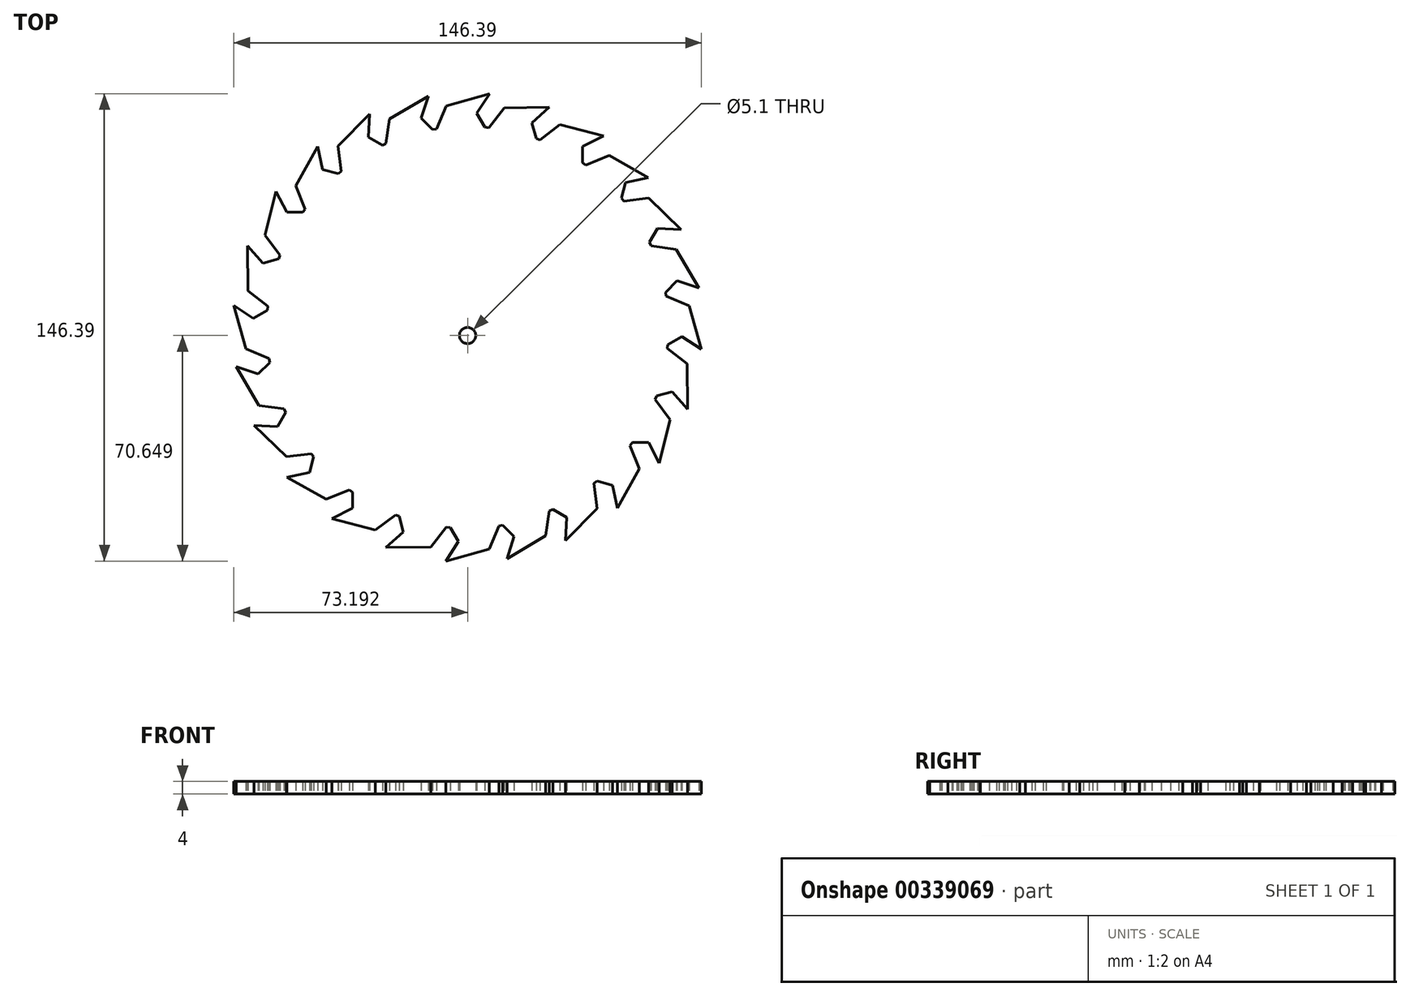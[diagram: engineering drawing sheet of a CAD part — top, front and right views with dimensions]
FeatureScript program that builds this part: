
annotation { "Feature Type Name" : "Feature", "Feature Type Description" : "" }
export const myFeature = defineFeature(function(context is Context, id is Id, definition is map)
    precondition{}
    {
        {
            var Q0;
            Q0=qCreatedBy(makeId("Top.planeOp"),FACE);
            var sketch = newSketch(context, id + "F0", { "sketchPlane" : qUnion([Q0])});
            skCircle(sketch, "E0", {"center": v(-75.15, 71.96) * mm, "radius": 61.72 * mm});
            skCircle(sketch, "E1", {"center": v(-75.15, 71.96) * mm, "radius": 2.55 * mm});
            skLineSegment(sketch, "E2", {"start": v(-121.66, 131.8) * mm, "end": v(-128.98, 118.83) * mm});
            skLineSegment(sketch, "E3", {"start": v(-128.98, 118.83) * mm, "end": v(-126.02, 111.53) * mm});
            skLineSegment(sketch, "E4", {"start": v(-126.02, 111.53) * mm, "end": v(-126.75, 110.54) * mm});
            skLineSegment(sketch, "E5", {"start": v(-126.75, 110.54) * mm, "end": v(-131.8, 110.54) * mm});
            skLineSegment(sketch, "E6", {"start": v(-131.8, 110.54) * mm, "end": v(-135.43, 117.68) * mm});
            skLineSegment(sketch, "E7.1.0", {"start": v(-134.9, 117.82) * mm, "end": v(-138.62, 103.38) * mm});
            skLineSegment(sketch, "E7.1.1", {"start": v(-138.62, 103.38) * mm, "end": v(-133.87, 97.1) * mm});
            skLineSegment(sketch, "E7.1.2", {"start": v(-134.32, 95.96) * mm, "end": v(-139.2, 94.65) * mm});
            skLineSegment(sketch, "E7.1.3", {"start": v(-133.87, 97.1) * mm, "end": v(-134.32, 95.96) * mm});
            skLineSegment(sketch, "E7.1.4", {"start": v(-139.2, 94.65) * mm, "end": v(-144.55, 100.6) * mm});
            skLineSegment(sketch, "E7.2.0", {"start": v(-144.08, 100.87) * mm, "end": v(-143.93, 85.97) * mm});
            skLineSegment(sketch, "E7.2.1", {"start": v(-143.93, 85.97) * mm, "end": v(-137.71, 81.14) * mm});
            skLineSegment(sketch, "E7.2.2", {"start": v(-137.86, 79.91) * mm, "end": v(-142.23, 77.39) * mm});
            skLineSegment(sketch, "E7.2.3", {"start": v(-137.71, 81.14) * mm, "end": v(-137.86, 79.91) * mm});
            skLineSegment(sketch, "E7.2.4", {"start": v(-142.23, 77.39) * mm, "end": v(-148.94, 81.76) * mm});
            skLineSegment(sketch, "E7.3.0", {"start": v(-148.55, 82.13) * mm, "end": v(-144.55, 67.78) * mm});
            skLineSegment(sketch, "E7.3.1", {"start": v(-144.55, 67.78) * mm, "end": v(-137.3, 64.72) * mm});
            skLineSegment(sketch, "E7.3.2", {"start": v(-137.12, 63.5) * mm, "end": v(-140.69, 59.93) * mm});
            skLineSegment(sketch, "E7.3.3", {"start": v(-137.3, 64.72) * mm, "end": v(-137.12, 63.5) * mm});
            skLineSegment(sketch, "E7.3.4", {"start": v(-140.69, 59.93) * mm, "end": v(-148.3, 62.41) * mm});
            skLineSegment(sketch, "E7.4.0", {"start": v(-148.03, 62.87) * mm, "end": v(-140.45, 50.05) * mm});
            skLineSegment(sketch, "E7.4.1", {"start": v(-140.45, 50.05) * mm, "end": v(-132.65, 48.97) * mm});
            skLineSegment(sketch, "E7.4.2", {"start": v(-132.16, 47.84) * mm, "end": v(-134.68, 43.46) * mm});
            skLineSegment(sketch, "E7.4.3", {"start": v(-132.65, 48.97) * mm, "end": v(-132.16, 47.84) * mm});
            skLineSegment(sketch, "E7.4.4", {"start": v(-134.68, 43.46) * mm, "end": v(-142.67, 43.9) * mm});
            skLineSegment(sketch, "E7.5.0", {"start": v(-142.53, 44.4) * mm, "end": v(-131.89, 33.98) * mm});
            skLineSegment(sketch, "E7.5.1", {"start": v(-131.89, 33.98) * mm, "end": v(-124.08, 34.96) * mm});
            skLineSegment(sketch, "E7.5.2", {"start": v(-123.31, 33.99) * mm, "end": v(-124.62, 29.11) * mm});
            skLineSegment(sketch, "E7.5.3", {"start": v(-124.08, 34.96) * mm, "end": v(-123.31, 33.99) * mm});
            skLineSegment(sketch, "E7.5.4", {"start": v(-124.62, 29.11) * mm, "end": v(-132.45, 27.46) * mm});
            skLineSegment(sketch, "E7.6.0", {"start": v(-132.45, 28) * mm, "end": v(-119.47, 20.67) * mm});
            skLineSegment(sketch, "E7.6.1", {"start": v(-119.47, 20.67) * mm, "end": v(-112.17, 23.64) * mm});
            skLineSegment(sketch, "E7.6.2", {"start": v(-111.18, 22.9) * mm, "end": v(-111.18, 17.86) * mm});
            skLineSegment(sketch, "E7.6.3", {"start": v(-112.17, 23.64) * mm, "end": v(-111.18, 22.9) * mm});
            skLineSegment(sketch, "E7.6.4", {"start": v(-111.18, 17.86) * mm, "end": v(-118.32, 14.23) * mm});
            skLineSegment(sketch, "E7.7.0", {"start": v(-118.45, 14.75) * mm, "end": v(-104.02, 11.04) * mm});
            skLineSegment(sketch, "E7.7.1", {"start": v(-104.02, 11.04) * mm, "end": v(-97.75, 15.79) * mm});
            skLineSegment(sketch, "E7.7.2", {"start": v(-96.6, 15.34) * mm, "end": v(-95.3, 10.46) * mm});
            skLineSegment(sketch, "E7.7.3", {"start": v(-97.75, 15.79) * mm, "end": v(-96.6, 15.34) * mm});
            skLineSegment(sketch, "E7.7.4", {"start": v(-95.3, 10.46) * mm, "end": v(-101.25, 5.11) * mm});
            skLineSegment(sketch, "E7.8.0", {"start": v(-101.51, 5.58) * mm, "end": v(-86.61, 5.73) * mm});
            skLineSegment(sketch, "E7.8.1", {"start": v(-86.61, 5.73) * mm, "end": v(-81.78, 11.94) * mm});
            skLineSegment(sketch, "E7.8.2", {"start": v(-80.55, 11.8) * mm, "end": v(-78.03, 7.43) * mm});
            skLineSegment(sketch, "E7.8.3", {"start": v(-81.78, 11.94) * mm, "end": v(-80.55, 11.8) * mm});
            skLineSegment(sketch, "E7.8.4", {"start": v(-78.03, 7.43) * mm, "end": v(-82.4, 0.72) * mm});
            skLineSegment(sketch, "E7.9.0", {"start": v(-82.77, 1.1) * mm, "end": v(-68.42, 5.1) * mm});
            skLineSegment(sketch, "E7.9.1", {"start": v(-68.42, 5.1) * mm, "end": v(-65.36, 12.36) * mm});
            skLineSegment(sketch, "E7.9.2", {"start": v(-64.14, 12.54) * mm, "end": v(-60.57, 8.97) * mm});
            skLineSegment(sketch, "E7.9.3", {"start": v(-65.36, 12.36) * mm, "end": v(-64.14, 12.54) * mm});
            skLineSegment(sketch, "E7.9.4", {"start": v(-60.57, 8.97) * mm, "end": v(-63.05, 1.36) * mm});
            skLineSegment(sketch, "E7.10.0", {"start": v(-63.51, 1.63) * mm, "end": v(-50.69, 9.21) * mm});
            skLineSegment(sketch, "E7.10.1", {"start": v(-50.69, 9.21) * mm, "end": v(-49.6, 17) * mm});
            skLineSegment(sketch, "E7.10.2", {"start": v(-48.47, 17.5) * mm, "end": v(-44.1, 14.98) * mm});
            skLineSegment(sketch, "E7.10.3", {"start": v(-49.6, 17) * mm, "end": v(-48.47, 17.5) * mm});
            skLineSegment(sketch, "E7.10.4", {"start": v(-44.1, 14.98) * mm, "end": v(-44.53, 6.98) * mm});
            skLineSegment(sketch, "E7.11.0", {"start": v(-45.05, 7.12) * mm, "end": v(-34.62, 17.77) * mm});
            skLineSegment(sketch, "E7.11.1", {"start": v(-34.62, 17.77) * mm, "end": v(-35.6, 25.58) * mm});
            skLineSegment(sketch, "E7.11.2", {"start": v(-34.63, 26.35) * mm, "end": v(-29.75, 25.04) * mm});
            skLineSegment(sketch, "E7.11.3", {"start": v(-35.6, 25.58) * mm, "end": v(-34.63, 26.35) * mm});
            skLineSegment(sketch, "E7.11.4", {"start": v(-29.75, 25.04) * mm, "end": v(-28.1, 17.2) * mm});
            skLineSegment(sketch, "E7.12.0", {"start": v(-28.63, 17.21) * mm, "end": v(-21.31, 30.2) * mm});
            skLineSegment(sketch, "E7.12.1", {"start": v(-21.31, 30.2) * mm, "end": v(-24.28, 37.48) * mm});
            skLineSegment(sketch, "E7.12.2", {"start": v(-23.54, 38.47) * mm, "end": v(-18.5, 38.47) * mm});
            skLineSegment(sketch, "E7.12.3", {"start": v(-24.28, 37.48) * mm, "end": v(-23.54, 38.47) * mm});
            skLineSegment(sketch, "E7.12.4", {"start": v(-18.5, 38.47) * mm, "end": v(-14.87, 31.34) * mm});
            skLineSegment(sketch, "E7.13.0", {"start": v(-15.39, 31.2) * mm, "end": v(-11.68, 45.63) * mm});
            skLineSegment(sketch, "E7.13.1", {"start": v(-11.68, 45.63) * mm, "end": v(-16.43, 51.91) * mm});
            skLineSegment(sketch, "E7.13.2", {"start": v(-15.97, 53.06) * mm, "end": v(-11.1, 54.37) * mm});
            skLineSegment(sketch, "E7.13.3", {"start": v(-16.43, 51.91) * mm, "end": v(-15.97, 53.06) * mm});
            skLineSegment(sketch, "E7.13.4", {"start": v(-11.1, 54.37) * mm, "end": v(-5.75, 48.4) * mm});
            skLineSegment(sketch, "E7.14.0", {"start": v(-6.22, 48.14) * mm, "end": v(-6.37, 63.04) * mm});
            skLineSegment(sketch, "E7.14.1", {"start": v(-6.37, 63.04) * mm, "end": v(-12.58, 67.88) * mm});
            skLineSegment(sketch, "E7.14.2", {"start": v(-12.44, 69.1) * mm, "end": v(-8.07, 71.63) * mm});
            skLineSegment(sketch, "E7.14.3", {"start": v(-12.58, 67.88) * mm, "end": v(-12.44, 69.1) * mm});
            skLineSegment(sketch, "E7.14.4", {"start": v(-8.07, 71.63) * mm, "end": v(-1.36, 67.26) * mm});
            skLineSegment(sketch, "E7.15.0", {"start": v(-1.74, 66.88) * mm, "end": v(-5.74, 81.24) * mm});
            skLineSegment(sketch, "E7.15.1", {"start": v(-5.74, 81.24) * mm, "end": v(-13, 84.3) * mm});
            skLineSegment(sketch, "E7.15.2", {"start": v(-13.18, 85.52) * mm, "end": v(-9.6, 89.09) * mm});
            skLineSegment(sketch, "E7.15.3", {"start": v(-13, 84.3) * mm, "end": v(-13.18, 85.52) * mm});
            skLineSegment(sketch, "E7.15.4", {"start": v(-9.6, 89.09) * mm, "end": v(-2, 86.6) * mm});
            skLineSegment(sketch, "E7.16.0", {"start": v(-2.27, 86.14) * mm, "end": v(-9.85, 98.97) * mm});
            skLineSegment(sketch, "E7.16.1", {"start": v(-9.85, 98.97) * mm, "end": v(-17.65, 100.05) * mm});
            skLineSegment(sketch, "E7.16.2", {"start": v(-18.14, 101.18) * mm, "end": v(-15.61, 105.56) * mm});
            skLineSegment(sketch, "E7.16.3", {"start": v(-17.65, 100.05) * mm, "end": v(-18.14, 101.18) * mm});
            skLineSegment(sketch, "E7.16.4", {"start": v(-15.61, 105.56) * mm, "end": v(-7.62, 105.13) * mm});
            skLineSegment(sketch, "E7.17.0", {"start": v(-7.76, 104.6) * mm, "end": v(-18.4, 115.04) * mm});
            skLineSegment(sketch, "E7.17.1", {"start": v(-18.4, 115.04) * mm, "end": v(-26.22, 114.06) * mm});
            skLineSegment(sketch, "E7.17.2", {"start": v(-26.98, 115.03) * mm, "end": v(-25.68, 119.9) * mm});
            skLineSegment(sketch, "E7.17.3", {"start": v(-26.22, 114.06) * mm, "end": v(-26.98, 115.03) * mm});
            skLineSegment(sketch, "E7.17.4", {"start": v(-25.68, 119.9) * mm, "end": v(-17.85, 121.56) * mm});
            skLineSegment(sketch, "E7.18.0", {"start": v(-17.85, 121.02) * mm, "end": v(-30.83, 128.34) * mm});
            skLineSegment(sketch, "E7.18.1", {"start": v(-30.83, 128.34) * mm, "end": v(-38.12, 125.38) * mm});
            skLineSegment(sketch, "E7.18.2", {"start": v(-39.11, 126.11) * mm, "end": v(-39.11, 131.16) * mm});
            skLineSegment(sketch, "E7.18.3", {"start": v(-38.12, 125.38) * mm, "end": v(-39.11, 126.11) * mm});
            skLineSegment(sketch, "E7.18.4", {"start": v(-39.11, 131.16) * mm, "end": v(-31.98, 134.79) * mm});
            skLineSegment(sketch, "E7.19.0", {"start": v(-31.84, 134.27) * mm, "end": v(-46.27, 137.98) * mm});
            skLineSegment(sketch, "E7.19.1", {"start": v(-46.27, 137.98) * mm, "end": v(-52.55, 133.23) * mm});
            skLineSegment(sketch, "E7.19.2", {"start": v(-53.7, 133.68) * mm, "end": v(-55, 138.56) * mm});
            skLineSegment(sketch, "E7.19.3", {"start": v(-52.55, 133.23) * mm, "end": v(-53.7, 133.68) * mm});
            skLineSegment(sketch, "E7.19.4", {"start": v(-55, 138.56) * mm, "end": v(-49.05, 143.9) * mm});
            skLineSegment(sketch, "E7.20.0", {"start": v(-48.78, 143.44) * mm, "end": v(-63.68, 143.3) * mm});
            skLineSegment(sketch, "E7.20.1", {"start": v(-63.68, 143.3) * mm, "end": v(-68.52, 137.08) * mm});
            skLineSegment(sketch, "E7.20.2", {"start": v(-69.74, 137.22) * mm, "end": v(-72.27, 141.59) * mm});
            skLineSegment(sketch, "E7.20.3", {"start": v(-68.52, 137.08) * mm, "end": v(-69.74, 137.22) * mm});
            skLineSegment(sketch, "E7.20.4", {"start": v(-72.27, 141.59) * mm, "end": v(-67.9, 148.3) * mm});
            skLineSegment(sketch, "E7.21.0", {"start": v(-67.52, 147.92) * mm, "end": v(-81.88, 143.91) * mm});
            skLineSegment(sketch, "E7.21.1", {"start": v(-81.88, 143.91) * mm, "end": v(-84.94, 136.66) * mm});
            skLineSegment(sketch, "E7.21.2", {"start": v(-86.16, 136.48) * mm, "end": v(-89.73, 140.05) * mm});
            skLineSegment(sketch, "E7.21.3", {"start": v(-84.94, 136.66) * mm, "end": v(-86.16, 136.48) * mm});
            skLineSegment(sketch, "E7.21.4", {"start": v(-89.73, 140.05) * mm, "end": v(-87.24, 147.66) * mm});
            skLineSegment(sketch, "E7.22.0", {"start": v(-86.78, 147.39) * mm, "end": v(-99.61, 139.8) * mm});
            skLineSegment(sketch, "E7.22.1", {"start": v(-99.61, 139.8) * mm, "end": v(-100.69, 132) * mm});
            skLineSegment(sketch, "E7.22.2", {"start": v(-101.82, 131.52) * mm, "end": v(-106.2, 134.04) * mm});
            skLineSegment(sketch, "E7.22.3", {"start": v(-100.69, 132) * mm, "end": v(-101.82, 131.52) * mm});
            skLineSegment(sketch, "E7.22.4", {"start": v(-106.2, 134.04) * mm, "end": v(-105.76, 142.04) * mm});
            skLineSegment(sketch, "E7.23.0", {"start": v(-105.25, 141.9) * mm, "end": v(-115.68, 131.25) * mm});
            skLineSegment(sketch, "E7.23.1", {"start": v(-115.68, 131.25) * mm, "end": v(-114.7, 123.44) * mm});
            skLineSegment(sketch, "E7.23.2", {"start": v(-115.67, 122.67) * mm, "end": v(-120.54, 123.98) * mm});
            skLineSegment(sketch, "E7.23.3", {"start": v(-114.7, 123.44) * mm, "end": v(-115.67, 122.67) * mm});
            skLineSegment(sketch, "E7.23.4", {"start": v(-120.54, 123.98) * mm, "end": v(-122.2, 131.81) * mm});
            skPoint(sketch, "E7.center", {"position": v(-75.15, 74.5) * mm});
            skSolve(sketch);
        }
        {
            var Q0;
            {var subQ53=sQuery(id+"F0.wireOp",EDGE,"E3");Q0=makeQuery(id+"F0.imprint","IMPRINT",FACE,{"disambiguationData":[TD([[makeQuery(id+"F0.imprint","IMPRINT",EDGE,{"derivedFrom":subQ53}),1.0]])]});}
            var Q1;
            Q1=makeQuery(id+"F0.imprint","IMPRINT",FACE,{"disambiguationData":[TD([[makeQuery(id+"F0.imprint","IMPRINT",EDGE,{"derivedFrom":sQuery(id+"F0.wireOp",EDGE,"E1")}),-1.0]])]});
            var Q2;
            {var subQ5=sQuery(id+"F0.wireOp",EDGE,"E7.5.2");var subQ7=sQuery(id+"F0.wireOp",EDGE,"E0");var subQ8=makeQuery(id+"F0.imprint","INTERSECT",VERTEX,{"derivedFrom":[subQ7,subQ5]});Q2=makeQuery(id+"F0.imprint","IMPRINT",FACE,{"disambiguationData":[TD([[makeQuery(id+"F0.imprint","IMPRINT",EDGE,{"disambiguationData":[TD([[subQ8,-1.0]])],"derivedFrom":subQ7}),-1.0]])]});}
            var Q3;
            {var subQ5=sQuery(id+"F0.wireOp",EDGE,"E7.6.2");var subQ7=sQuery(id+"F0.wireOp",EDGE,"E0");var subQ8=makeQuery(id+"F0.imprint","INTERSECT",VERTEX,{"derivedFrom":[subQ7,subQ5]});Q3=makeQuery(id+"F0.imprint","IMPRINT",FACE,{"disambiguationData":[TD([[makeQuery(id+"F0.imprint","IMPRINT",EDGE,{"disambiguationData":[TD([[subQ8,-1.0]])],"derivedFrom":subQ7}),-1.0]])]});}
            var Q4;
            {var subQ5=sQuery(id+"F0.wireOp",EDGE,"E7.7.2");var subQ7=sQuery(id+"F0.wireOp",EDGE,"E0");var subQ8=makeQuery(id+"F0.imprint","INTERSECT",VERTEX,{"derivedFrom":[subQ7,subQ5]});Q4=makeQuery(id+"F0.imprint","IMPRINT",FACE,{"disambiguationData":[TD([[makeQuery(id+"F0.imprint","IMPRINT",EDGE,{"disambiguationData":[TD([[subQ8,-1.0]])],"derivedFrom":subQ7}),-1.0]])]});}
            var Q5;
            {var subQ5=sQuery(id+"F0.wireOp",EDGE,"E7.8.2");var subQ7=sQuery(id+"F0.wireOp",EDGE,"E0");var subQ8=makeQuery(id+"F0.imprint","INTERSECT",VERTEX,{"derivedFrom":[subQ7,subQ5]});Q5=makeQuery(id+"F0.imprint","IMPRINT",FACE,{"disambiguationData":[TD([[makeQuery(id+"F0.imprint","IMPRINT",EDGE,{"disambiguationData":[TD([[subQ8,-1.0]])],"derivedFrom":subQ7}),-1.0]])]});}
            var Q6;
            {var subQ5=sQuery(id+"F0.wireOp",EDGE,"E7.9.2");var subQ6=sQuery(id+"F0.wireOp",EDGE,"E0");var subQ7=makeQuery(id+"F0.imprint","INTERSECT",VERTEX,{"derivedFrom":[subQ6,subQ5]});Q6=makeQuery(id+"F0.imprint","IMPRINT",FACE,{"disambiguationData":[TD([[makeQuery(id+"F0.imprint","IMPRINT",EDGE,{"disambiguationData":[TD([[subQ7,-1.0]])],"derivedFrom":subQ6}),-1.0]])]});}
            var Q7;
            {var subQ5=sQuery(id+"F0.wireOp",EDGE,"E7.10.2");var subQ7=sQuery(id+"F0.wireOp",EDGE,"E0");var subQ8=makeQuery(id+"F0.imprint","INTERSECT",VERTEX,{"derivedFrom":[subQ7,subQ5]});Q7=makeQuery(id+"F0.imprint","IMPRINT",FACE,{"disambiguationData":[TD([[makeQuery(id+"F0.imprint","IMPRINT",EDGE,{"disambiguationData":[TD([[subQ8,-1.0]])],"derivedFrom":subQ7}),-1.0]])]});}
            var Q8;
            {var subQ5=sQuery(id+"F0.wireOp",EDGE,"E7.11.2");var subQ7=sQuery(id+"F0.wireOp",EDGE,"E0");var subQ8=makeQuery(id+"F0.imprint","INTERSECT",VERTEX,{"derivedFrom":[subQ7,subQ5]});Q8=makeQuery(id+"F0.imprint","IMPRINT",FACE,{"disambiguationData":[TD([[makeQuery(id+"F0.imprint","IMPRINT",EDGE,{"disambiguationData":[TD([[subQ8,-1.0]])],"derivedFrom":subQ7}),-1.0]])]});}
            extrude(context, id + "F1", {"entities" : qUnion([Q0, Q1, Q2, Q3, Q4, Q5, Q6, Q7, Q8]), "depth" : 4 * mm, "offsetDistance" : 25 * mm});
        }
    });
